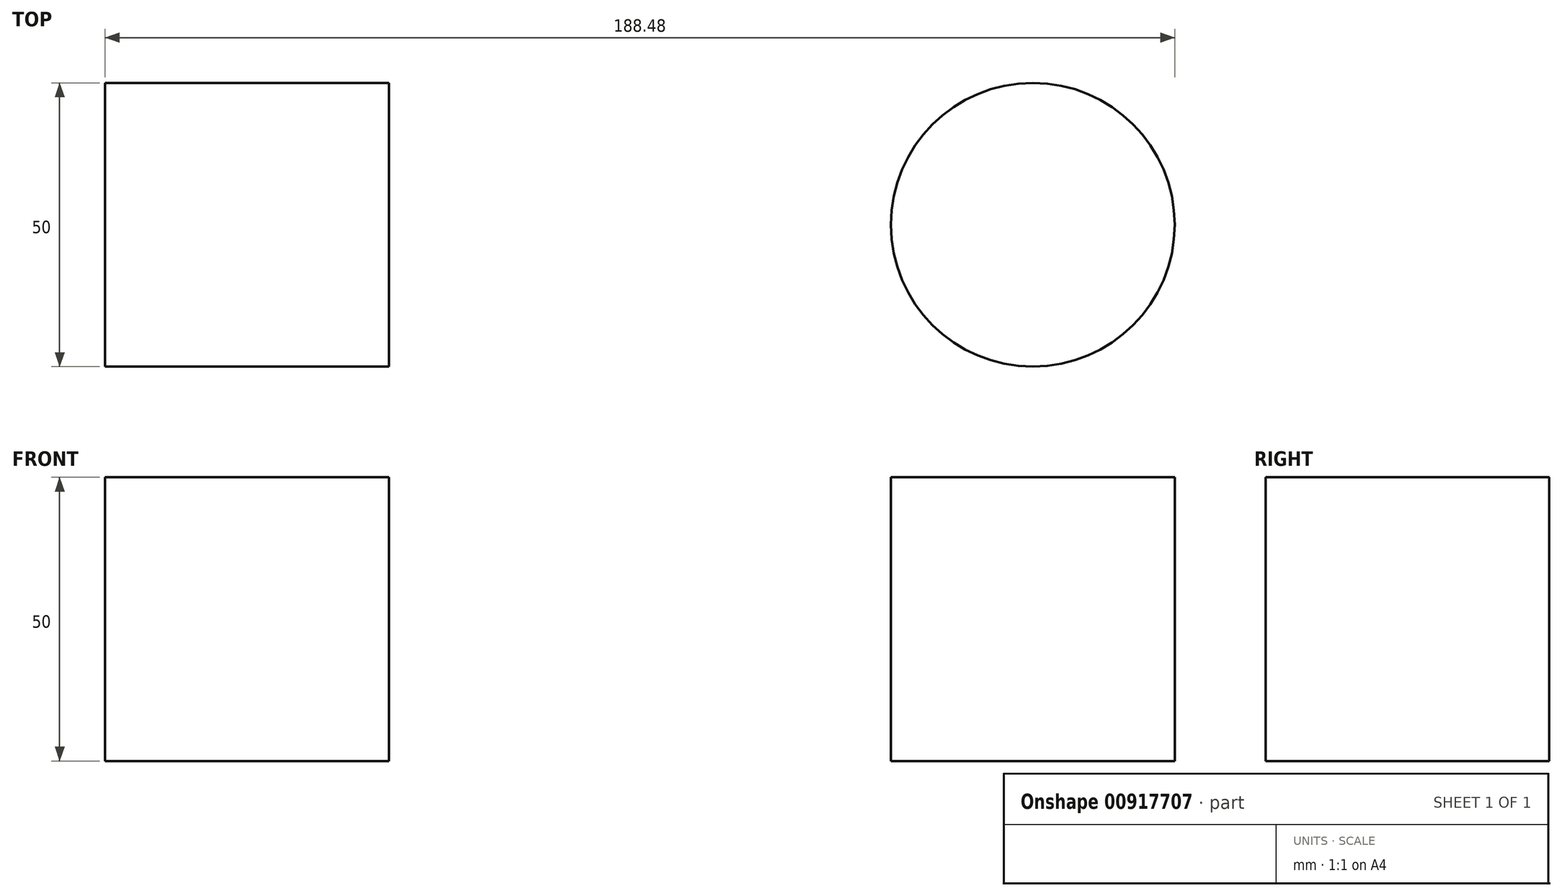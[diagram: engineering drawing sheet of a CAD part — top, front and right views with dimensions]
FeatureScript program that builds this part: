
annotation { "Feature Type Name" : "Feature", "Feature Type Description" : "" }
export const myFeature = defineFeature(function(context is Context, id is Id, definition is map)
    precondition{}
    {
        {
            var Q0;
            Q0=qCreatedBy(makeId("Top.planeOp"),FACE);
            var sketch = newSketch(context, id + "F0", { "sketchPlane" : qUnion([Q0])});
            skLineSegment(sketch, "E0.bottom", {"start": v(-84.45, 19.59) * mm, "end": v(-134.45, 19.59) * mm});
            skLineSegment(sketch, "E0.top", {"start": v(-84.45, 69.59) * mm, "end": v(-134.45, 69.59) * mm});
            skLineSegment(sketch, "E0.left", {"start": v(-84.45, 19.59) * mm, "end": v(-84.45, 69.59) * mm});
            skLineSegment(sketch, "E0.right", {"start": v(-134.45, 19.59) * mm, "end": v(-134.45, 69.59) * mm});
            skPoint(sketch, "E0.middle", {"position": v(-109.45, 44.59) * mm});
            skCircle(sketch, "E1", {"center": v(29.03, 44.59) * mm, "radius": 25 * mm});
            skSolve(sketch);
        }
        {
            var Q0;
            Q0=makeQuery(id+"F0.imprint","IMPRINT",FACE,{"disambiguationData":[TD([[makeQuery(id+"F0.imprint","IMPRINT",EDGE,{"derivedFrom":sQuery(id+"F0.wireOp",EDGE,"E0.bottom")}),-1.0]])]});
            extrude(context, id + "F1", {"entities" : qUnion([Q0]), "depth" : 50 * mm, "offsetDistance" : 25 * mm});
        }
        {
            var Q0;
            Q0 = qSketchRegion(id + "F0", true);
            extrude(context, id + "F2", {"entities" : qUnion([Q0]), "operationType" : NewBodyOperationType.ADD, "depth" : 50 * mm, "offsetDistance" : 25 * mm});
        }
    });
